# Revit family: FP-Revit20-en-RF505ANUX1-RefrigeratorFreezer-90006114A-UK-IE
name_source: partatom
category: Specialty Equipment
units: mm (PartAtom-declared; Revit-internal decimal feet)

## family parameters
Always vertical = Yes
Cut with Voids When Loaded = Yes
Part Type = Normal
Room Calculation Point = No
Round Connector Dimension = Use Diameter
Shared = No
Work Plane-Based = No

## types (1)
- RF505ANUX1
    Chassis = Fisher & Paykel - Aluminium
    Clearance = Fisher & Paykel - Clearance Required (Non-Combustible)
    Clearance - Vent = Fisher & Paykel - Clearance Required (Non-Combustible)
    Clearance Cavity = Yes
    Default Elevation = 0 mm  [stored 0 ft]
    Description = French Door Refrigerator Freezer with Water and Ice
    Door swing = Yes
    Electrical Specifications = Supply: 220V - 240V, 50Hz, Service: 10A circuit
    Handle finish = Fisher & Paykel - Grey, Charcoal
    Left side clearance = 20 mm  [stored 0.0656168 ft]
    Manufacturer = Fisher & Paykel
    Model = RF505ANUX1
    Plumbing Specifications = Water Supply: 1/4" LLDPE piping, Pressure: Max 827 kPa (120 psi) @ 68°F (20°C)
    Product depth = 707 mm
    Product height = 1725 mm  [stored 5.65945 ft]
    Product width = 790 mm  [stored 2.59186 ft]
    Rear clearance = 30 mm  [stored 0.0984252 ft]
    Right side clearance = 20 mm  [stored 0.0656168 ft]
    Top vent clearance = 50 mm  [stored 0.164042 ft]
    URL = www.fisherpaykel.com
    Vent clearance (see planning guide for options) = Yes
    Water Dispenser material = Fisher & Paykel - Black, Matte

note: [stored X ft] marks values corroborated as IEEE doubles in the binary element streams (Revit-internal decimal feet)

## geometry (parser evidence)
native form markers: Sweep x16
no freeform markers — native parametric forms only
